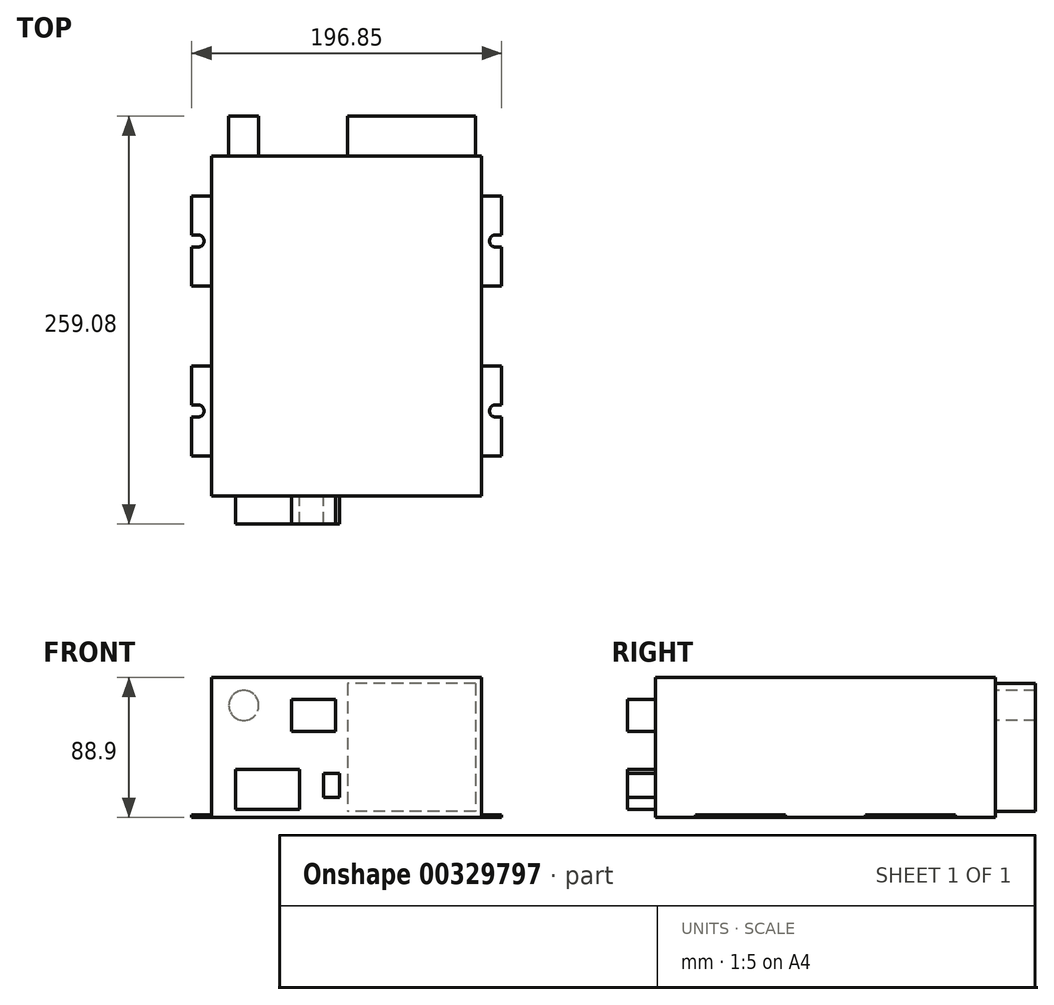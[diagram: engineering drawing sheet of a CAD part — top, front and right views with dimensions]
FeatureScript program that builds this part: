
annotation { "Feature Type Name" : "Feature", "Feature Type Description" : "" }
export const myFeature = defineFeature(function(context is Context, id is Id, definition is map)
    precondition{}
    {
        {
            var Q0;
            Q0=qCreatedBy(makeId("Front.planeOp"),FACE);
            var sketch = newSketch(context, id + "F0", { "sketchPlane" : qUnion([Q0])});
            skLineSegment(sketch, "E0.bottom", {"start": v(0, 0) * mm, "end": v(-171.45, 0) * mm});
            skLineSegment(sketch, "E0.top", {"start": v(0, 88.9) * mm, "end": v(-171.45, 88.9) * mm});
            skLineSegment(sketch, "E0.left", {"start": v(0, 0) * mm, "end": v(0, 88.9) * mm});
            skLineSegment(sketch, "E0.right", {"start": v(-171.45, 0) * mm, "end": v(-171.45, 88.9) * mm});
            skSolve(sketch);
        }
        {
            var Q0;
            Q0 = qSketchRegion(id + "F0", true);
            extrude(context, id + "F1", {"entities" : qUnion([Q0]), "depth" : 215.9 * mm});
        }
        {
            var Q0;
            Q0=makeQuery(id+"F1.opExtrude","CAP_FACE",FACE,{"disambiguationData":[OSD([sQuery(id+"F0.wireOp",EDGE,"E0.bottom"),sQuery(id+"F0.wireOp",EDGE,"E0.top"),sQuery(id+"F0.wireOp",EDGE,"E0.left"),sQuery(id+"F0.wireOp",EDGE,"E0.right")])],"isStart":false});
            var sketch = newSketch(context, id + "F2", { "sketchPlane" : qUnion([Q0])});
            skLineSegment(sketch, "E1.bottom", {"start": v(-156.21, 30.48) * mm, "end": v(-115.57, 30.48) * mm});
            skLineSegment(sketch, "E1.top", {"start": v(-156.21, 5.08) * mm, "end": v(-115.57, 5.08) * mm});
            skLineSegment(sketch, "E1.left", {"start": v(-156.21, 30.48) * mm, "end": v(-156.21, 5.08) * mm});
            skLineSegment(sketch, "E1.right", {"start": v(-115.57, 30.48) * mm, "end": v(-115.57, 5.08) * mm});
            skLineSegment(sketch, "E2.bottom", {"start": v(-120.65, 74.93) * mm, "end": v(-92.7, 74.93) * mm});
            skLineSegment(sketch, "E2.top", {"start": v(-120.65, 54.6) * mm, "end": v(-92.7, 54.6) * mm});
            skLineSegment(sketch, "E2.left", {"start": v(-120.65, 74.93) * mm, "end": v(-120.65, 54.6) * mm});
            skLineSegment(sketch, "E2.right", {"start": v(-92.7, 74.93) * mm, "end": v(-92.7, 54.6) * mm});
            skLineSegment(sketch, "E3.bottom", {"start": v(-100.33, 27.94) * mm, "end": v(-90.17, 27.94) * mm});
            skLineSegment(sketch, "E3.top", {"start": v(-100.33, 12.7) * mm, "end": v(-90.17, 12.7) * mm});
            skLineSegment(sketch, "E3.left", {"start": v(-100.33, 27.94) * mm, "end": v(-100.33, 12.7) * mm});
            skLineSegment(sketch, "E3.right", {"start": v(-90.17, 27.94) * mm, "end": v(-90.17, 12.7) * mm});
            skSolve(sketch);
        }
        {
            var Q0;
            Q0 = qSketchRegion(id + "F2", true);
            extrude(context, id + "F3", {"entities" : qUnion([Q0]), "operationType" : NewBodyOperationType.ADD, "depth" : 17.78 * mm});
        }
        {
            var Q0;
            Q0=makeQuery(id+"F1.opExtrude","CAP_FACE",FACE,{"disambiguationData":[OSD([sQuery(id+"F0.wireOp",EDGE,"E0.bottom"),sQuery(id+"F0.wireOp",EDGE,"E0.top"),sQuery(id+"F0.wireOp",EDGE,"E0.left"),sQuery(id+"F0.wireOp",EDGE,"E0.right")])],"isStart":true});
            var sketch = newSketch(context, id + "F4", { "sketchPlane" : qUnion([Q0])});
            skLineSegment(sketch, "E4.bottom", {"start": v(3.81, 85.1) * mm, "end": v(85.1, 85.1) * mm});
            skLineSegment(sketch, "E4.top", {"start": v(3.81, 3.8) * mm, "end": v(85.1, 3.8) * mm});
            skLineSegment(sketch, "E4.left", {"start": v(3.8, 85.1) * mm, "end": v(3.81, 3.8) * mm});
            skLineSegment(sketch, "E4.right", {"start": v(85.1, 85.1) * mm, "end": v(85.1, 3.8) * mm});
            skCircle(sketch, "E5", {"center": v(151.13, 71.12) * mm, "radius": 9.53 * mm});
            skSolve(sketch);
        }
        {
            var Q0;
            Q0 = qSketchRegion(id + "F4", true);
            extrude(context, id + "F5", {"entities" : qUnion([Q0]), "operationType" : NewBodyOperationType.ADD, "depth" : 25.4 * mm});
        }
        {
            var Q0;
            Q0=makeQuery(id+"F1.opExtrude","SWEPT_FACE",FACE,{"disambiguationData":[OSD([sQuery(id+"F0.wireOp",EDGE,"E0.bottom")])]});
            var sketch = newSketch(context, id + "F6", { "sketchPlane" : qUnion([Q0])});
            skLineSegment(sketch, "E6.bottom", {"start": v(0, 25.4) * mm, "end": v(12.7, 25.4) * mm});
            skLineSegment(sketch, "E6.top", {"start": v(0, 82.55) * mm, "end": v(12.7, 82.55) * mm});
            skLineSegment(sketch, "E6.right", {"start": v(12.7, 25.4) * mm, "end": v(12.7, 50.16) * mm});
            skArc(sketch, "E7", {"start": v(8.74, 57.78) * mm, "mid": v(4.93, 53.97) * mm, "end": v(8.74, 50.16) * mm});
            skLineSegment(sketch, "E8", {"start": v(8.74, 50.16) * mm, "end": v(12.7, 50.16) * mm});
            skLineSegment(sketch, "E9", {"start": v(8.74, 57.78) * mm, "end": v(12.7, 57.78) * mm});
            skLineSegment(sketch, "E10.trimOffspring", {"start": v(12.7, 57.78) * mm, "end": v(12.7, 82.55) * mm});
            skLineSegment(sketch, "E11.bottom", {"start": v(0, 133.35) * mm, "end": v(12.7, 133.35) * mm});
            skLineSegment(sketch, "E11.top", {"start": v(0, 190.5) * mm, "end": v(12.7, 190.5) * mm});
            skLineSegment(sketch, "E11.right", {"start": v(12.7, 133.35) * mm, "end": v(12.7, 158.11) * mm});
            skArc(sketch, "E12", {"start": v(8.74, 165.73) * mm, "mid": v(4.93, 161.92) * mm, "end": v(8.74, 158.11) * mm});
            skLineSegment(sketch, "E13", {"start": v(8.74, 158.11) * mm, "end": v(12.7, 158.11) * mm});
            skLineSegment(sketch, "E14", {"start": v(8.74, 165.73) * mm, "end": v(12.7, 165.73) * mm});
            skLineSegment(sketch, "E15.trimOffspring", {"start": v(12.7, 165.73) * mm, "end": v(12.7, 190.5) * mm});
            skLineSegment(sketch, "E16.bottom", {"start": v(-171.45, 190.5) * mm, "end": v(-184.15, 190.5) * mm});
            skLineSegment(sketch, "E16.top", {"start": v(-171.45, 133.35) * mm, "end": v(-184.15, 133.35) * mm});
            skLineSegment(sketch, "E16.right", {"start": v(-184.15, 190.5) * mm, "end": v(-184.15, 165.73) * mm});
            skArc(sketch, "E17", {"start": v(-180.19, 158.11) * mm, "mid": v(-176.38, 161.92) * mm, "end": v(-180.19, 165.73) * mm});
            skLineSegment(sketch, "E18", {"start": v(-180.19, 165.73) * mm, "end": v(-184.15, 165.73) * mm});
            skLineSegment(sketch, "E19", {"start": v(-180.19, 158.11) * mm, "end": v(-184.15, 158.11) * mm});
            skLineSegment(sketch, "E20.trimOffspring", {"start": v(-184.15, 158.11) * mm, "end": v(-184.15, 133.35) * mm});
            skLineSegment(sketch, "E21.bottom", {"start": v(-171.45, 82.55) * mm, "end": v(-184.15, 82.55) * mm});
            skLineSegment(sketch, "E21.top", {"start": v(-171.45, 25.4) * mm, "end": v(-184.15, 25.4) * mm});
            skLineSegment(sketch, "E21.right", {"start": v(-184.15, 82.55) * mm, "end": v(-184.15, 57.78) * mm});
            skArc(sketch, "E22", {"start": v(-180.19, 50.16) * mm, "mid": v(-176.38, 53.97) * mm, "end": v(-180.19, 57.78) * mm});
            skLineSegment(sketch, "E23", {"start": v(-180.19, 57.78) * mm, "end": v(-184.15, 57.78) * mm});
            skLineSegment(sketch, "E24", {"start": v(-180.19, 50.16) * mm, "end": v(-184.15, 50.16) * mm});
            skLineSegment(sketch, "E25.trimOffspring", {"start": v(-184.15, 50.16) * mm, "end": v(-184.15, 25.4) * mm});
            skSolve(sketch);
        }
        {
            var Q0;
            {var subQ1=sQuery(id+"F6.wireOp",EDGE,"E21.bottom");Q0=makeQuery(id+"F6.imprint","IMPRINT",FACE,{"disambiguationData":[TD([[makeQuery(id+"F6.imprint","IMPRINT",EDGE,{"derivedFrom":subQ1}),1.0]])]});}
            var Q1;
            {var subQ0=sQuery(id+"F6.wireOp",EDGE,"E16.bottom");Q1=makeQuery(id+"F6.imprint","IMPRINT",FACE,{"disambiguationData":[TD([[makeQuery(id+"F6.imprint","IMPRINT",EDGE,{"derivedFrom":subQ0}),1.0]])]});}
            var Q2;
            {var subQ1=sQuery(id+"F6.wireOp",EDGE,"E11.bottom");Q2=makeQuery(id+"F6.imprint","IMPRINT",FACE,{"disambiguationData":[TD([[makeQuery(id+"F6.imprint","IMPRINT",EDGE,{"derivedFrom":subQ1}),1.0]])]});}
            var Q3;
            {var subQ1=sQuery(id+"F6.wireOp",EDGE,"E6.bottom");Q3=makeQuery(id+"F6.imprint","IMPRINT",FACE,{"disambiguationData":[TD([[makeQuery(id+"F6.imprint","IMPRINT",EDGE,{"derivedFrom":subQ1}),1.0]])]});}
            extrude(context, id + "F7", {"entities" : qUnion([Q0, Q1, Q2, Q3]), "operationType" : NewBodyOperationType.ADD, "oppositeDirection" : true, "depth" : 1.52 * mm});
        }
    });
